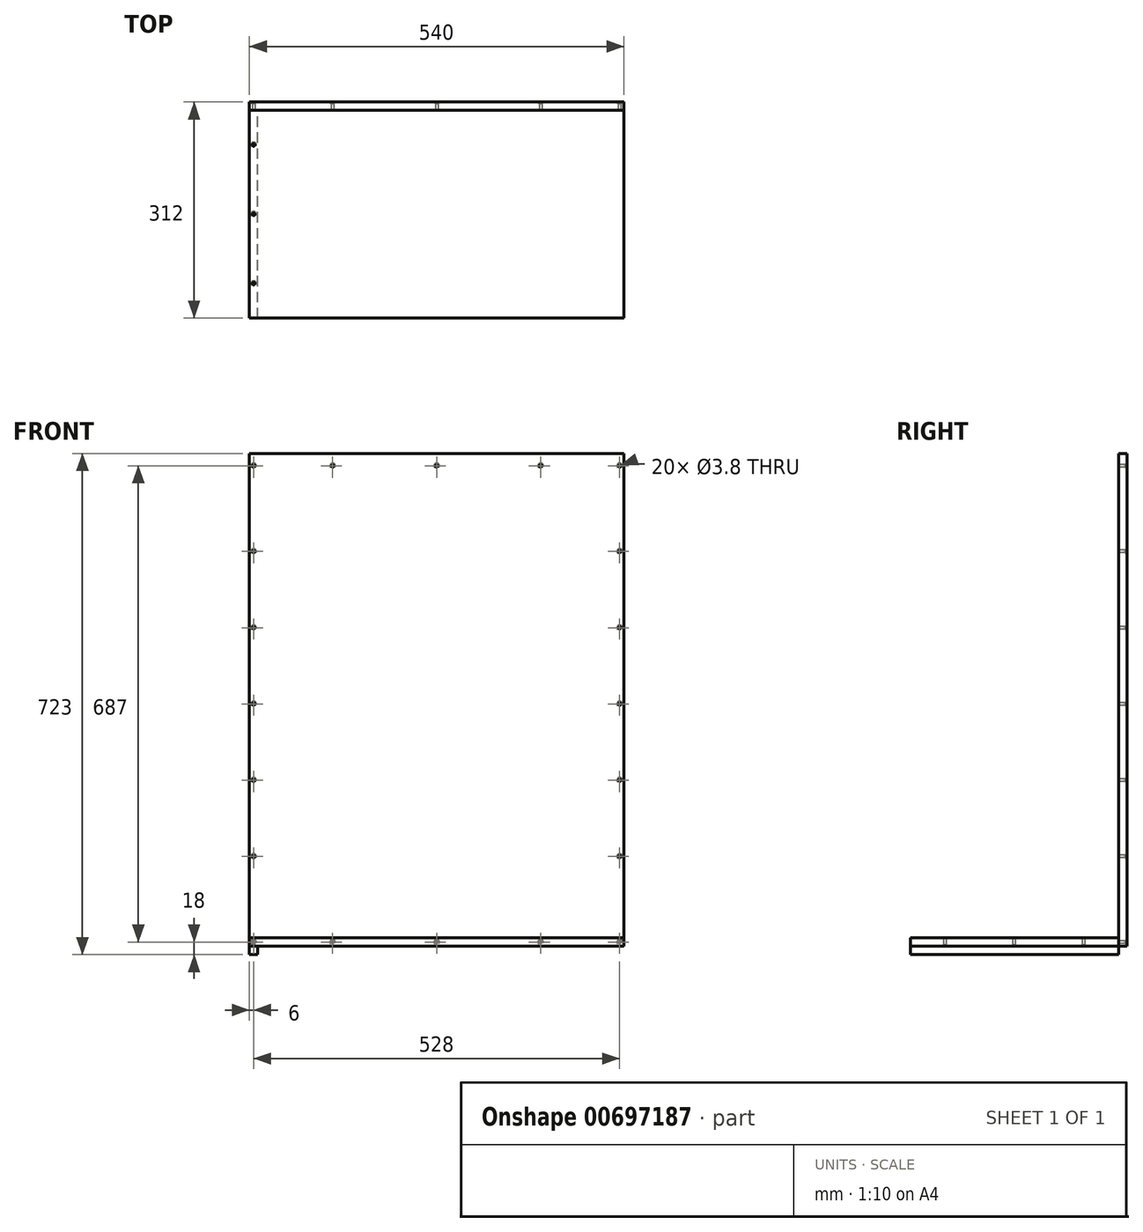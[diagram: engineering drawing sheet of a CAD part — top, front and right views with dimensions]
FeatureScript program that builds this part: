
annotation { "Feature Type Name" : "Feature", "Feature Type Description" : "" }
export const myFeature = defineFeature(function(context is Context, id is Id, definition is map)
    precondition{}
    {
        {
            var Q0;
            Q0=qCreatedBy(makeId("Top.planeOp"),FACE);
            var sketch = newSketch(context, id + "F0", { "sketchPlane" : qUnion([Q0])});
            skLineSegment(sketch, "E0.bottom", {"start": v(270, -150) * mm, "end": v(-270, -150) * mm});
            skLineSegment(sketch, "E0.top", {"start": v(270, 150) * mm, "end": v(-270, 150) * mm});
            skLineSegment(sketch, "E0.left", {"start": v(270, -150) * mm, "end": v(270, 150) * mm});
            skLineSegment(sketch, "E0.right", {"start": v(-270, -150) * mm, "end": v(-270, 150) * mm});
            skPoint(sketch, "E0.middle", {"position": v(0, 0) * mm});
            skSolve(sketch);
        }
        {
            var Q0;
            Q0 = qSketchRegion(id + "F0", true);
            extrude(context, id + "F1", {"entities" : qUnion([Q0]), "depth" : 12 * mm, "offsetDistance" : 25 * mm});
        }
        {
            var Q0;
            Q0=makeQuery(id+"F1.opExtrude","CAP_FACE",FACE,{"disambiguationData":[OSD([sQuery(id+"F0.wireOp",EDGE,"E0.bottom"),sQuery(id+"F0.wireOp",EDGE,"E0.top"),sQuery(id+"F0.wireOp",EDGE,"E0.left"),sQuery(id+"F0.wireOp",EDGE,"E0.right")])],"isStart":true});
            var sketch = newSketch(context, id + "F2", { "sketchPlane" : qUnion([Q0])});
            skPoint(sketch, "E1", {"position": v(-264, -100) * mm});
            skLineSegment(sketch, "E2", {"start": v(-264, -100) * mm, "end": v(-264, 34.15) * mm, "construction": true});
            skPoint(sketch, "E3", {"position": v(-264, 0) * mm});
            skPoint(sketch, "E4.MirrorP", {"position": v(-264, 100) * mm});
            skSolve(sketch);
        }
        {
            var Q0;
            Q0=sQuery(id+"F2.wireOp",VERTEX,"E1");
            var Q1;
            Q1=sQuery(id+"F2.wireOp",VERTEX,"E3");
            var Q2;
            Q2=sQuery(id+"F2.wireOp",VERTEX,"E4.MirrorP");
            var Q3;
            Q3=makeQuery(id+"F1.opExtrude","SWEPT_BODY",BODY,{"disambiguationData":[OSD([sQuery(id+"F0.wireOp",EDGE,"E0.bottom"),sQuery(id+"F0.wireOp",EDGE,"E0.top"),sQuery(id+"F0.wireOp",EDGE,"E0.left"),sQuery(id+"F0.wireOp",EDGE,"E0.right")])]});
            hole(context, id + "F3", {"style" : HoleStyle.C_SINK, "endStyle" : HoleEndStyle.THROUGH, "standardTappedOrClearance" : lookupTablePath({ "standard" : "ANSI", "fit" : "Normal (ASME)", "size" : "#6", "type" : "Clearance" }), "standardBlindInLast" : lookupTablePath({ "fit" : "Free", "standard" : "ANSI", "size" : "#6", "type" : "Clearance" }), "holeDiameter" : 3.8 * mm, "cSinkDiameter" : 7.8 * mm, "cSinkAngle" : 82 * degree, "majorDiameter" : 5 * mm, "isTappedThrough" : true, "tappedDepth" : 12 * mm, "tapClearance" : 3, "locations" : qUnion([Q0, Q1, Q2]), "scope" : qUnion([Q3]), "startStyle" : HoleStartStyle.SKETCH});
        }
        {
            var Q0;
            Q0=makeQuery(id+"F1.opExtrude","SWEPT_FACE",FACE,{"disambiguationData":[OSD([sQuery(id+"F0.wireOp",EDGE,"E0.top")])]});
            var sketch = newSketch(context, id + "F4", { "sketchPlane" : qUnion([Q0])});
            skLineSegment(sketch, "E5.0", {"start": v(-270, 0) * mm, "end": v(270, 0) * mm});
            skLineSegment(sketch, "E6.0", {"start": v(-270, 699) * mm, "end": v(-270, 0) * mm});
            skLineSegment(sketch, "E7.0", {"start": v(270, 699) * mm, "end": v(270, 0) * mm});
            skLineSegment(sketch, "E8", {"start": v(270, 699) * mm, "end": v(-270, 699) * mm});
            skPoint(sketch, "E9.orphan", {"position": v(270, 12) * mm});
            skPoint(sketch, "E10.orphan", {"position": v(-270, 12) * mm});
            skSolve(sketch);
        }
        {
            var Q0;
            Q0 = qSketchRegion(id + "F4", true);
            extrude(context, id + "F5", {"entities" : qUnion([Q0]), "depth" : 12 * mm, "offsetDistance" : 25 * mm});
        }
        {
            var Q0;
            Q0=makeQuery(id+"F5.opExtrude","CAP_FACE",FACE,{"disambiguationData":[OSD([sQuery(id+"F4.wireOp",EDGE,"E5.0"),sQuery(id+"F4.wireOp",EDGE,"E6.0"),sQuery(id+"F4.wireOp",EDGE,"E7.0"),sQuery(id+"F4.wireOp",EDGE,"E8")])],"isStart":false});
            var sketch = newSketch(context, id + "F6", { "sketchPlane" : qUnion([Q0])});
            skLineSegment(sketch, "E11.bottom", {"start": v(-264, 693) * mm, "end": v(264, 693) * mm, "construction": true});
            skLineSegment(sketch, "E11.top", {"start": v(-264, 6) * mm, "end": v(264, 6) * mm, "construction": true});
            skLineSegment(sketch, "E11.left", {"start": v(-264, 693) * mm, "end": v(-264, 6) * mm, "construction": true});
            skLineSegment(sketch, "E11.right", {"start": v(264, 693) * mm, "end": v(264, 6) * mm, "construction": true});
            skPoint(sketch, "E12", {"position": v(264, 349.5) * mm});
            skPoint(sketch, "E13", {"position": v(264, 459.5) * mm});
            skPoint(sketch, "E14", {"position": v(264, 569.5) * mm});
            skPoint(sketch, "E15", {"position": v(264, 239.5) * mm});
            skPoint(sketch, "E16", {"position": v(264, 129.5) * mm});
            skPoint(sketch, "E17", {"position": v(264, 693) * mm});
            skPoint(sketch, "E18", {"position": v(264, 6) * mm});
            skPoint(sketch, "E19", {"position": v(-264, 6) * mm});
            skPoint(sketch, "E20", {"position": v(-264, 693) * mm});
            skPoint(sketch, "E21", {"position": v(-264, 349.5) * mm});
            skPoint(sketch, "E22", {"position": v(0, 693) * mm});
            skPoint(sketch, "E23", {"position": v(0, 6) * mm});
            skPoint(sketch, "E24", {"position": v(150, 6) * mm});
            skPoint(sketch, "E25", {"position": v(-150, 6) * mm});
            skPoint(sketch, "E26", {"position": v(-264, 129.5) * mm});
            skPoint(sketch, "E27", {"position": v(-264, 239.5) * mm});
            skPoint(sketch, "E28", {"position": v(-264, 459.5) * mm});
            skPoint(sketch, "E29", {"position": v(-264, 569.5) * mm});
            skPoint(sketch, "E30", {"position": v(-150, 693) * mm});
            skPoint(sketch, "E31", {"position": v(150, 693) * mm});
            skSolve(sketch);
        }
        {
            var Q0;
            Q0=sQuery(id+"F6.wireOp",VERTEX,"E16");
            var Q1;
            Q1=sQuery(id+"F6.wireOp",VERTEX,"E15");
            var Q2;
            Q2=sQuery(id+"F6.wireOp",VERTEX,"E12");
            var Q3;
            Q3=sQuery(id+"F6.wireOp",VERTEX,"E13");
            var Q4;
            Q4=sQuery(id+"F6.wireOp",VERTEX,"E14");
            var Q5;
            Q5=sQuery(id+"F6.wireOp",VERTEX,"E17");
            var Q6;
            Q6=sQuery(id+"F6.wireOp",VERTEX,"E31");
            var Q7;
            Q7=sQuery(id+"F6.wireOp",VERTEX,"E22");
            var Q8;
            Q8=sQuery(id+"F6.wireOp",VERTEX,"E30");
            var Q9;
            Q9=sQuery(id+"F6.wireOp",VERTEX,"E20");
            var Q10;
            Q10=sQuery(id+"F6.wireOp",VERTEX,"E29");
            var Q11;
            Q11=sQuery(id+"F6.wireOp",VERTEX,"E28");
            var Q12;
            Q12=sQuery(id+"F6.wireOp",VERTEX,"E21");
            var Q13;
            Q13=sQuery(id+"F6.wireOp",VERTEX,"E27");
            var Q14;
            Q14=sQuery(id+"F6.wireOp",VERTEX,"E26");
            var Q15;
            Q15=sQuery(id+"F6.wireOp",VERTEX,"E19");
            var Q16;
            Q16=sQuery(id+"F6.wireOp",VERTEX,"E25");
            var Q17;
            Q17=sQuery(id+"F6.wireOp",VERTEX,"E23");
            var Q18;
            Q18=sQuery(id+"F6.wireOp",VERTEX,"E24");
            var Q19;
            Q19=sQuery(id+"F6.wireOp",VERTEX,"E18");
            var Q20;
            Q20=makeQuery(id+"F5.opExtrude","SWEPT_BODY",BODY,{"disambiguationData":[OSD([sQuery(id+"F4.wireOp",EDGE,"E5.0"),sQuery(id+"F4.wireOp",EDGE,"E6.0"),sQuery(id+"F4.wireOp",EDGE,"E7.0"),sQuery(id+"F4.wireOp",EDGE,"E8")])]});
            hole(context, id + "F7", {"style" : HoleStyle.C_SINK, "endStyle" : HoleEndStyle.THROUGH, "standardTappedOrClearance" : lookupTablePath({ "standard" : "ANSI", "fit" : "Normal (ASME)", "size" : "#6", "type" : "Clearance" }), "standardBlindInLast" : lookupTablePath({ "fit" : "Free", "standard" : "ANSI", "size" : "#6", "type" : "Clearance" }), "holeDiameter" : 3.8 * mm, "cSinkDiameter" : 7.8 * mm, "cSinkAngle" : 82 * degree, "majorDiameter" : 5 * mm, "isTappedThrough" : true, "tappedDepth" : 12 * mm, "tapClearance" : 3, "locations" : qUnion([Q0, Q1, Q2, Q3, Q4, Q5, Q6, Q7, Q8, Q9, Q10, Q11, Q12, Q13, Q14, Q15, Q16, Q17, Q18, Q19]), "scope" : qUnion([Q20]), "startStyle" : HoleStartStyle.SKETCH});
        }
        {
            var Q0;
            Q0=makeQuery(id+"F5.opExtrude","SWEPT_FACE",FACE,{"disambiguationData":[OSD([sQuery(id+"F4.wireOp",EDGE,"E8")])]});
            extrude(context, id + "F8", {"entities" : qUnion([Q0]), "operationType" : NewBodyOperationType.ADD, "depth" : 12 * mm, "offsetDistance" : 25 * mm});
        }
        {
            var Q0;
            Q0=makeQuery(id+"F1.opExtrude","CAP_FACE",FACE,{"disambiguationData":[OSD([sQuery(id+"F0.wireOp",EDGE,"E0.bottom"),sQuery(id+"F0.wireOp",EDGE,"E0.top"),sQuery(id+"F0.wireOp",EDGE,"E0.left"),sQuery(id+"F0.wireOp",EDGE,"E0.right")])],"isStart":true});
            var sketch = newSketch(context, id + "F9", { "sketchPlane" : qUnion([Q0])});
            skLineSegment(sketch, "E32.0", {"start": v(-270, 150) * mm, "end": v(-270, -150) * mm});
            skLineSegment(sketch, "E33.0", {"start": v(-258, 150) * mm, "end": v(-270, 150) * mm});
            skLineSegment(sketch, "E34.0", {"start": v(-258, -150) * mm, "end": v(-270, -150) * mm});
            skLineSegment(sketch, "E35", {"start": v(-258, 150) * mm, "end": v(-258, -150) * mm});
            skSolve(sketch);
        }
        {
            var Q0;
            Q0 = qSketchRegion(id + "F9", true);
            extrude(context, id + "F10", {"entities" : qUnion([Q0]), "depth" : 12 * mm, "offsetDistance" : 25 * mm});
        }
    });
